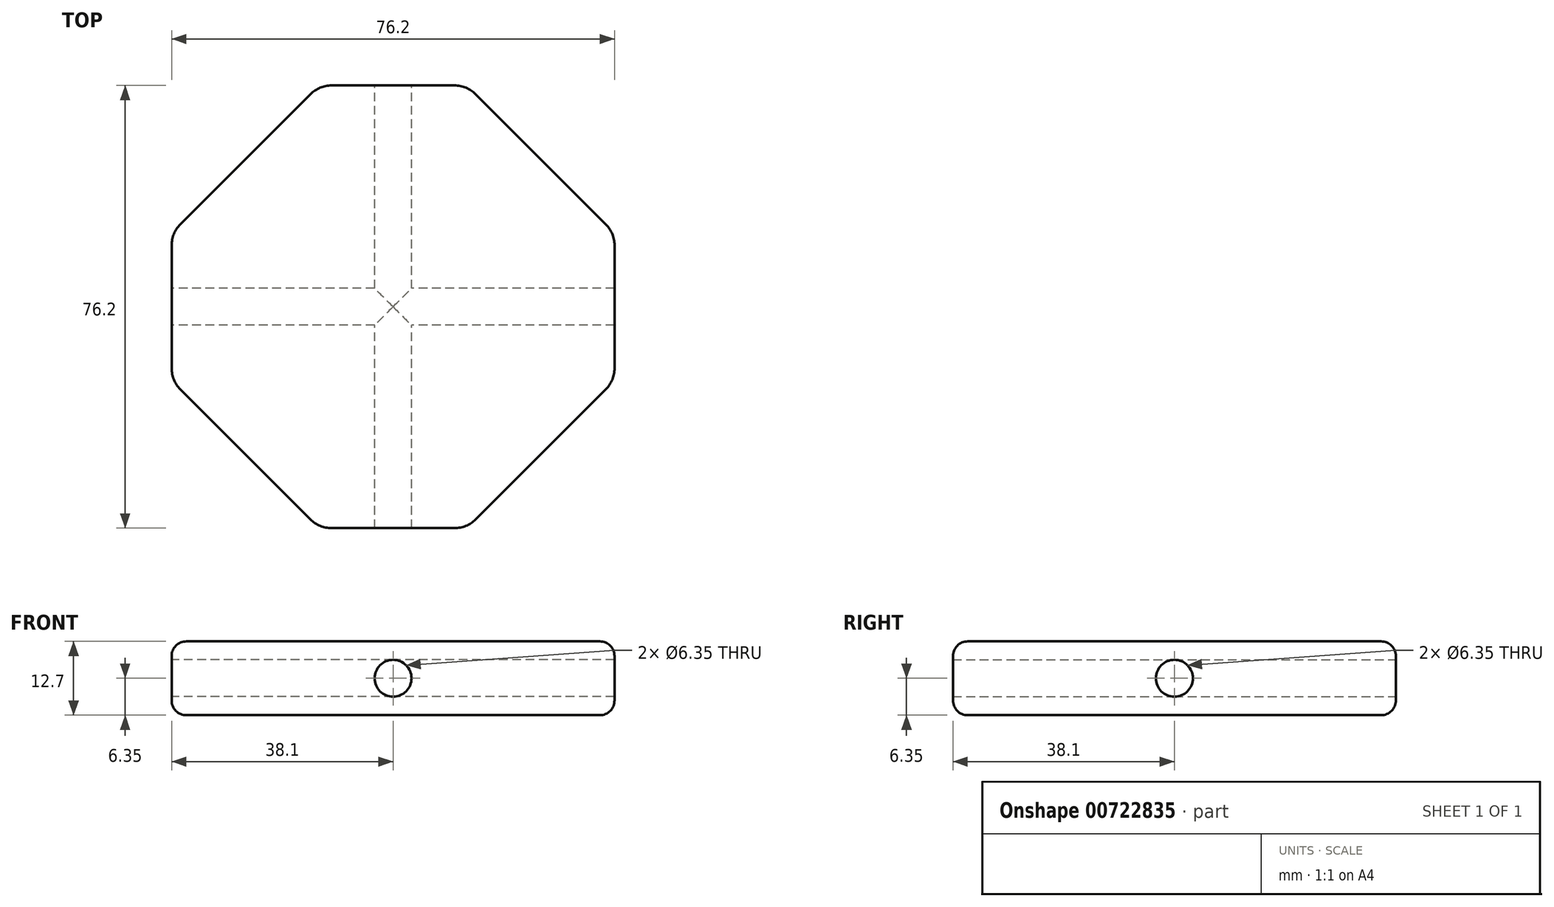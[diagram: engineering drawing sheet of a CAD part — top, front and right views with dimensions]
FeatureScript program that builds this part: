
annotation { "Feature Type Name" : "Feature", "Feature Type Description" : "" }
export const myFeature = defineFeature(function(context is Context, id is Id, definition is map)
    precondition{}
    {
        {
            var Q0;
            Q0=qCreatedBy(makeId("Top.planeOp"),FACE);
            var sketch = newSketch(context, id + "F0", { "sketchPlane" : qUnion([Q0])});
            skLineSegment(sketch, "E0", {"start": v(-38.1, 12.7) * mm, "end": v(-38.1, -12.7) * mm});
            skLineSegment(sketch, "E1", {"start": v(-12.7, -38.1) * mm, "end": v(12.7, -38.1) * mm});
            skLineSegment(sketch, "E2", {"start": v(38.1, -12.7) * mm, "end": v(38.1, 12.7) * mm});
            skLineSegment(sketch, "E3", {"start": v(38.1, 12.7) * mm, "end": v(12.7, 38.1) * mm});
            skLineSegment(sketch, "E4", {"start": v(12.7, 38.1) * mm, "end": v(-12.7, 38.1) * mm});
            skLineSegment(sketch, "E5", {"start": v(-12.7, 38.1) * mm, "end": v(-38.1, 12.7) * mm});
            skLineSegment(sketch, "E6", {"start": v(-38.1, -12.7) * mm, "end": v(-12.7, -38.1) * mm});
            skLineSegment(sketch, "E7", {"start": v(12.7, -38.1) * mm, "end": v(38.1, -12.7) * mm});
            skPoint(sketch, "E8.orphan", {"position": v(-38.1, -38.1) * mm});
            skPoint(sketch, "E9.orphan", {"position": v(38.1, -38.1) * mm});
            skSolve(sketch);
        }
        {
            var Q0;
            Q0=makeQuery(id+"F0.imprint","IMPRINT",FACE,{"disambiguationData":[TD([[makeQuery(id+"F0.imprint","IMPRINT",EDGE,{"derivedFrom":sQuery(id+"F0.wireOp",EDGE,"E0")}),1.0]])]});
            extrude(context, id + "F1", {"entities" : qUnion([Q0]), "endBound" : BoundingType.SYMMETRIC, "depth" : 12.7 * mm, "offsetDistance" : 25.4 * mm});
        }
        {
            var Q0;
            Q0=makeQuery(id+"F1.opExtrude","SWEPT_FACE",FACE,{"disambiguationData":[OSD([sQuery(id+"F0.wireOp",EDGE,"E0")])]});
            var sketch = newSketch(context, id + "F2", { "sketchPlane" : qUnion([Q0])});
            skCircle(sketch, "E10", {"center": v(0, 0) * mm, "radius": 3.18 * mm});
            skSolve(sketch);
        }
        {
            var Q0;
            Q0=sQuery(id+"F2.wireOp",VERTEX,"E10.center");
            var Q1;
            Q1=makeQuery(id+"F1.opExtrude","SWEPT_BODY",BODY,{"disambiguationData":[OSD([sQuery(id+"F0.wireOp",EDGE,"E0"),sQuery(id+"F0.wireOp",EDGE,"E1"),sQuery(id+"F0.wireOp",EDGE,"E2"),sQuery(id+"F0.wireOp",EDGE,"E3"),sQuery(id+"F0.wireOp",EDGE,"E4"),sQuery(id+"F0.wireOp",EDGE,"E5")])]});
            hole(context, id + "F3", {"style" : HoleStyle.SIMPLE, "endStyle" : HoleEndStyle.THROUGH, "holeDiameter" : 6.35 * mm, "majorDiameter" : 6.35 * mm, "isTappedThrough" : true, "tappedDepth" : 12.7 * mm, "tapClearance" : 3, "locations" : qUnion([Q0]), "scope" : qUnion([Q1])});
        }
        {
            var Q0;
            Q0=makeQuery(id+"F1.opExtrude","SWEPT_EDGE",EDGE,{"disambiguationData":[OSD([sQuery(id+"F0.wireOp",EDGE,"E4"),sQuery(id+"F0.wireOp",EDGE,"E5")])]});
            var Q1;
            Q1=makeQuery(id+"F1.opExtrude","SWEPT_EDGE",EDGE,{"disambiguationData":[OSD([sQuery(id+"F0.wireOp",EDGE,"E0"),sQuery(id+"F0.wireOp",EDGE,"E5")])]});
            var Q2;
            Q2=makeQuery(id+"F1.opExtrude","SWEPT_EDGE",EDGE,{"disambiguationData":[OSD([sQuery(id+"F0.wireOp",EDGE,"E0"),sQuery(id+"F0.wireOp",EDGE,"E1")])]});
            var Q3;
            Q3=makeQuery(id+"F1.opExtrude","SWEPT_EDGE",EDGE,{"disambiguationData":[OSD([sQuery(id+"F0.wireOp",EDGE,"E3"),sQuery(id+"F0.wireOp",EDGE,"E4")])]});
            var Q4;
            Q4=makeQuery(id+"F1.opExtrude","SWEPT_EDGE",EDGE,{"disambiguationData":[OSD([sQuery(id+"F0.wireOp",EDGE,"E2"),sQuery(id+"F0.wireOp",EDGE,"E3")])]});
            var Q5;
            Q5=makeQuery(id+"F1.opExtrude","SWEPT_EDGE",EDGE,{"disambiguationData":[OSD([sQuery(id+"F0.wireOp",EDGE,"E1"),sQuery(id+"F0.wireOp",EDGE,"E2")])]});
            fillet(context, id + "F4", {"entities" : qUnion([Q0, Q1, Q2, Q3, Q4, Q5]), "radius" : 5.08 * mm, "tangentPropagation" : true, "allowEdgeOverflow" : false});
        }
        {
            var Q0;
            Q0=makeQuery(id+"F1.opExtrude","CAP_FACE",FACE,{"disambiguationData":[OSD([sQuery(id+"F0.wireOp",EDGE,"E0"),sQuery(id+"F0.wireOp",EDGE,"E1"),sQuery(id+"F0.wireOp",EDGE,"E2"),sQuery(id+"F0.wireOp",EDGE,"E3"),sQuery(id+"F0.wireOp",EDGE,"E4"),sQuery(id+"F0.wireOp",EDGE,"E5")])],"isStart":false});
            var Q1;
            Q1=makeQuery(id+"F1.opExtrude","CAP_FACE",FACE,{"disambiguationData":[OSD([sQuery(id+"F0.wireOp",EDGE,"E0"),sQuery(id+"F0.wireOp",EDGE,"E1"),sQuery(id+"F0.wireOp",EDGE,"E2"),sQuery(id+"F0.wireOp",EDGE,"E3"),sQuery(id+"F0.wireOp",EDGE,"E4"),sQuery(id+"F0.wireOp",EDGE,"E5")])],"isStart":true});
            fillet(context, id + "F5", {"entities" : qUnion([Q0, Q1]), "radius" : 2.54 * mm, "tangentPropagation" : true, "allowEdgeOverflow" : false});
        }
        {
            var Q0;
            Q0=makeQuery(id+"F1.opExtrude","SWEPT_FACE",FACE,{"disambiguationData":[OSD([sQuery(id+"F0.wireOp",EDGE,"E4")])]});
            var sketch = newSketch(context, id + "F6", { "sketchPlane" : qUnion([Q0])});
            skCircle(sketch, "E11", {"center": v(0, 0) * mm, "radius": 3.18 * mm});
            skSolve(sketch);
        }
        {
            var Q0;
            Q0=sQuery(id+"F6.wireOp",VERTEX,"E11.center");
            var Q1;
            Q1=makeQuery(id+"F1.opExtrude","SWEPT_BODY",BODY,{"disambiguationData":[OSD([sQuery(id+"F0.wireOp",EDGE,"E0"),sQuery(id+"F0.wireOp",EDGE,"E1"),sQuery(id+"F0.wireOp",EDGE,"E2"),sQuery(id+"F0.wireOp",EDGE,"E3"),sQuery(id+"F0.wireOp",EDGE,"E4"),sQuery(id+"F0.wireOp",EDGE,"E5")])]});
            hole(context, id + "F7", {"style" : HoleStyle.SIMPLE, "endStyle" : HoleEndStyle.THROUGH, "holeDiameter" : 6.35 * mm, "majorDiameter" : 6.35 * mm, "isTappedThrough" : true, "tappedDepth" : 12.7 * mm, "tapClearance" : 3, "locations" : qUnion([Q0]), "scope" : qUnion([Q1])});
        }
    });
